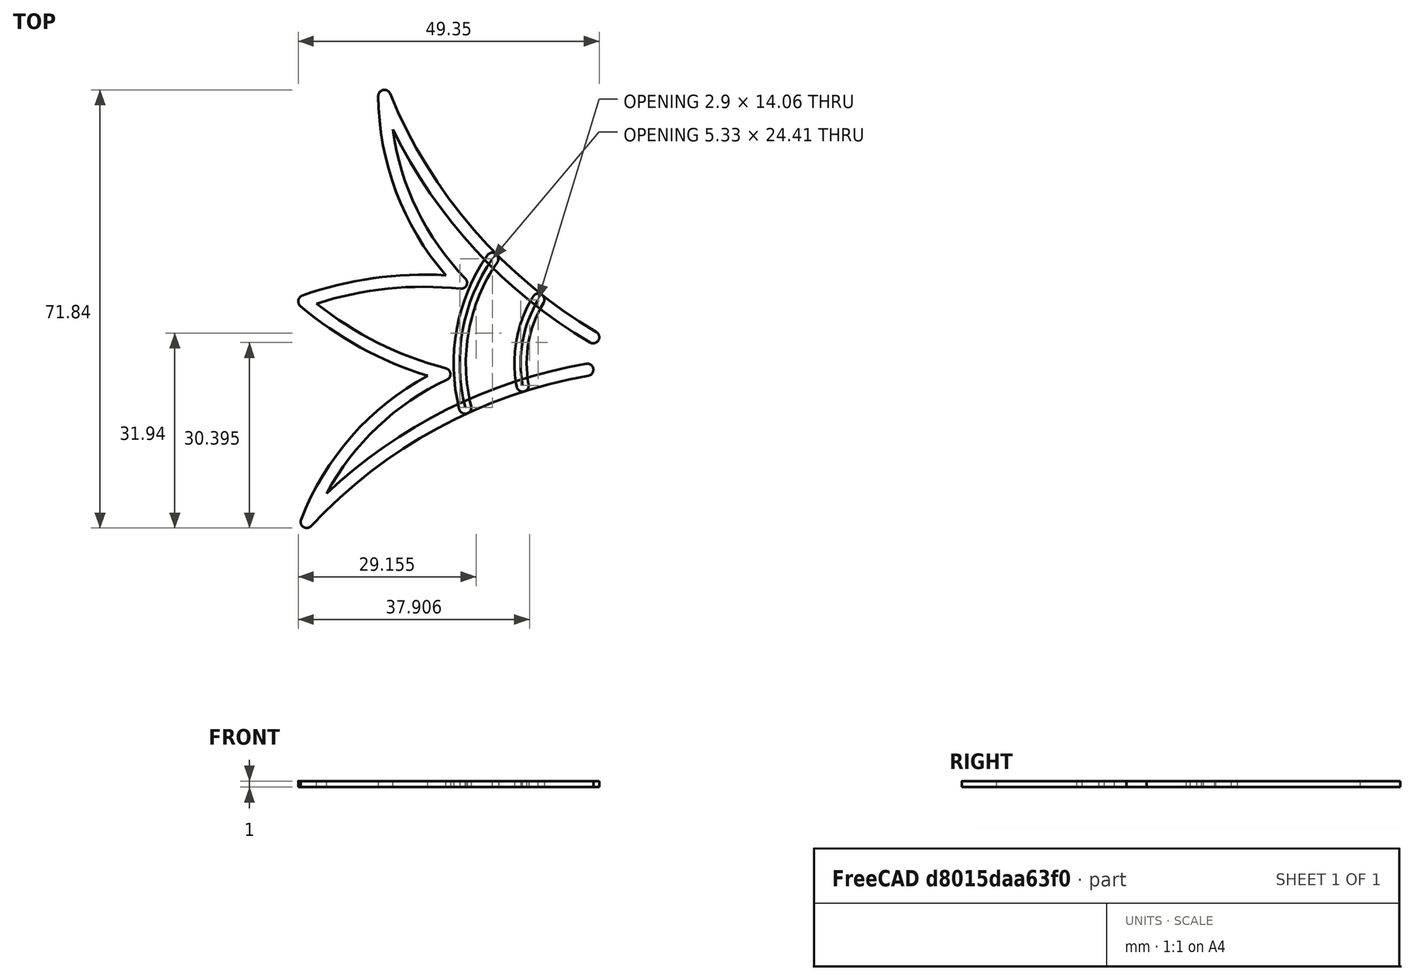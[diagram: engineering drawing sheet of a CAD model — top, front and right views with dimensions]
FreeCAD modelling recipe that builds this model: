
FCSTD DOCUMENT  (FreeCAD 0.20R27319 (Git))
Label: Bookend_1
License: All rights reserved
LicenseURL: http://en.wikipedia.org/wiki/All_rights_reserved
objects: Sketcher::SketchObject×2, TechDraw::DrawViewDimension×2, PartDesign::Body×1, PartDesign::Pad×1, Part::Offset2D×1, Part::Extrusion×1, PartDesign::Plane×1, Part::Mirroring×1, TechDraw::DrawSVGTemplate×1, TechDraw::DrawViewPart×1, TechDraw::DrawPage×1
note: 9 computed .brp shape members not serialized (recipe doc carries the construction recipe); baked Part::Feature solids carry a one-line shape summary decoded from their .brp

FEATURE [PartDesign::Body] Body001  label="Body"
  Origin = -> Origin001
FEATURE [Sketcher::SketchObject] Sketch001
  FullyConstrained = true
  MapMode = 5
  Support = -> [XY_Plane001]
  sketch-geometry (13):
    g0: LineSegment StartX=0 StartY=0 StartZ=0 EndX=150 EndY=-9e-16 EndZ=0
    g1: LineSegment StartX=0 StartY=0 StartZ=0 EndX=0 EndY=150 EndZ=0
    g2: LineSegment StartX=0 StartY=150 StartZ=0 EndX=150 EndY=0 EndZ=0
    g3: LineSegment StartX=0 StartY=0 StartZ=0 EndX=79.9497 EndY=79.9497 EndZ=0
    g4: GeomPoint X=29.9813 Y=120.019 Z=0
    g5: GeomPoint X=90.0373 Y=59.9627 Z=0
    g6: GeomPoint X=120.019 Y=29.9813 Z=0
    g7: ArcOfCircle CenterX=54.6331 CenterY=54.6331 CenterZ=0 NormalX=0 NormalY=0 NormalZ=1 AngleXU=0 Radius=35.8031 StartAngle=0.149412 EndAngle=1.42138
    g8: ArcOfCircle CenterX=125.429 CenterY=65.3732 CenterZ=0 NormalX=0 NormalY=0 NormalZ=1 AngleXU=0 Radius=35.8031 StartAngle=3.29329 EndAngle=4.56069
    g9: ArcOfCircle CenterX=114.608 CenterY=-5.41059 CenterZ=0 NormalX=0 NormalY=0 NormalZ=1 AngleXU=0 Radius=35.8031 StartAngle=0.151702 EndAngle=1.41909
    g10: ArcOfCircle CenterX=65.3732 CenterY=125.429 CenterZ=0 NormalX=0 NormalY=0 NormalZ=1 AngleXU=0 Radius=35.8031 StartAngle=3.29329 EndAngle=4.56069
    g11: ArcOfCircle CenterX=-5.41059 CenterY=114.608 CenterZ=0 NormalX=0 NormalY=0 NormalZ=1 AngleXU=0 Radius=35.8031 StartAngle=0.151702 EndAngle=1.41909
    g12: LineSegment StartX=75 StartY=75 StartZ=0 EndX=79.9497 EndY=79.9497 EndZ=0
  constraints (35):
    c: Coincident(g0,g-1)
    c: PointOnObject(g0,g-1)
    c: Distance(g0) = 150
    c: Coincident(g1,g0)
    c: PointOnObject(g1,g-2)
    c: Distance(g1) = 150
    c: Coincident(g2,g1)
    c: Coincident(g2,g0)
    c: Coincident(g3,g0)
    c: Angle(g0,g3) = 0.785398
    c: PointOnObject(g4,g2)
    c: Distance(g4,g1) = 42.4
    c: PointOnObject(g5,g2)
    c: PointOnObject(g6,g2)
    c: Distance(g5,g6) = 42.4
    c: Coincident(g7,g5)
    c: Coincident(g9,g0)
    c: Coincident(g11,g1)
    c: Coincident(g11,g4)
    c: Coincident(g5,g8)
    c: Coincident(g9,g8)
    c: Coincident(g8,g6)
    c: Coincident(g4,g10)
    c: Coincident(g10,g7)
    c: PointOnObject(g7,g2)
    c: Equal(g11,g10)
    c: Equal(g10,g7)
    c: Equal(g7,g8)
    c: Equal(g8,g9)
    c: Symmetric(g10,g8,g3)
    c: PointOnObject(g12,g3)
    c: PointOnObject(g12,g7)
    c: PointOnObject(g12,g2)
    c: Distance(g12,g12) = 7
    c: Coincident(g3,g12)
FEATURE [PartDesign::Pad] Pad
  Direction = (0,0,1)
  Length = 10
  Length2 = 10
  Profile = -> Sketch001
  ReferenceAxis = -> Sketch001 [N_Axis]
  Type = 0
FEATURE [Sketcher::SketchObject] Sketch
  ExternalGeometry = -> [Sketch001]
  FullyConstrained = false
  MapMode = 5
  Placement = pos=(0,0,10) rot=(0,0,1;0rad)
  Support = -> [Pad]
  sketch-geometry (13):
    g0: LineSegment StartX=0 StartY=150 StartZ=0 EndX=150 EndY=0 EndZ=0
    g1: LineSegment StartX=0 StartY=0 StartZ=0 EndX=75 EndY=75 EndZ=0
    g2: LineSegment StartX=77 StartY=0 StartZ=0 EndX=65.7983 EndY=59.5038 EndZ=0
    g3: ArcOfCircle CenterX=21.5521 CenterY=23.2682 CenterZ=0 NormalX=0 NormalY=0 NormalZ=1 AngleXU=0 Radius=57.9689 StartAngle=5.94509 EndAngle=6.39511
    g4: ArcOfCircle CenterX=109.889 CenterY=61.6651 CenterZ=0 NormalX=0 NormalY=0 NormalZ=1 AngleXU=0 Radius=44.31 StartAngle=3.94601 EndAngle=4.71162
    g5: ArcOfCircle CenterX=140.644 CenterY=93.6374 CenterZ=0 NormalX=0 NormalY=0 NormalZ=1 AngleXU=0 Radius=82.2616 StartAngle=3.6814 EndAngle=4.32876
    g6: ArcOfCircle CenterX=120.192 CenterY=41.8372 CenterZ=0 NormalX=0 NormalY=0 NormalZ=1 AngleXU=0 Radius=57.9689 StartAngle=3.40181 EndAngle=3.85183
    g7: ArcOfCircle CenterX=23.9401 CenterY=45.4852 CenterZ=0 NormalX=0 NormalY=0 NormalZ=1 AngleXU=0 Radius=44.31 StartAngle=5.08531 EndAngle=5.85092
    g8: ArcOfCircle CenterX=-16.3356 CenterY=64.0858 CenterZ=0 NormalX=0 NormalY=0 NormalZ=1 AngleXU=0 Radius=82.2616 StartAngle=5.46816 EndAngle=6.11552
    g9: ArcOfCircle CenterX=65.7983 CenterY=59.5038 CenterZ=0 NormalX=0 NormalY=0 NormalZ=1 AngleXU=0 Radius=20.0707 StartAngle=4.53436 EndAngle=5.26256
    g10: ArcOfCircle CenterX=65.7983 CenterY=59.5038 CenterZ=0 NormalX=0 NormalY=0 NormalZ=1 AngleXU=0 Radius=20.0707 StartAngle=4.53436 EndAngle=5.26256
    g11: ArcOfCircle CenterX=65.7983 CenterY=59.5038 CenterZ=0 NormalX=0 NormalY=0 NormalZ=1 AngleXU=0 Radius=30.0524 StartAngle=4.47297 EndAngle=5.32396
    g12: ArcOfCircle CenterX=65.7983 CenterY=59.5038 CenterZ=0 NormalX=0 NormalY=0 NormalZ=1 AngleXU=0 Radius=30.0524 StartAngle=4.47297 EndAngle=5.32396
  constraints (30):
    c: Coincident(g0,g-3)
    c: Coincident(g0,g-4)
    c: Coincident(g1,g-1)
    c: PointOnObject(g1,g0)
    c: Perpendicular(g0,g1)
    c: PointOnObject(g2,g-1)
    c: DistanceX(g1,g2) = 77
    c: Coincident(g4,g3)
    c: Coincident(g5,g4)
    c: Coincident(g6,g3)
    c: Coincident(g7,g6)
    c: Symmetric(g6,g3,g2)
    c: Coincident(g8,g7)
    c: Symmetric(g8,g5,g2)
    c: Symmetric(g6,g3,g2)
    c: Symmetric(g4,g7,g2)
    c: Symmetric(g8,g5,g2)
    c: PointOnObject(g2,g8)
    c: Coincident(g9,g2)
    c: PointOnObject(g9,g8)
    c: PointOnObject(g9,g5)
    c: Coincident(g10,g9)
    c: Coincident(g10,g9)
    c: Coincident(g10,g9)
    c: Coincident(g11,g9)
    c: PointOnObject(g11,g8)
    c: PointOnObject(g11,g5)
    c: Coincident(g12,g9)
    c: Coincident(g12,g11)
    c: Coincident(g12,g11)
FEATURE [Part::Offset2D] Offset2D
  Fill = true
  Intersection = false
  Join = 0
  Mode = 1
  SelfIntersection = false
  Source = -> Sketch
  Value = 1
FEATURE [Part::Extrusion] Extrude
  Base = -> Offset2D
  Dir = (0,0,1)
  DirMode = 2
  FaceMakerClass = Part::FaceMakerBullseye
  LengthFwd = 1
  LengthRev = 0
  Solid = false
  Symmetric = false
FEATURE [PartDesign::Plane] DatumPlane
  AttachmentOffset = pos=(0,0,0) rot=(0,1,0;0.785398rad)
  Length = 283.998
  MapMode = 5
  Placement = pos=(0,0,0) rot=(0.862856,0.357407,0.357407;1.71777rad)
  ResizeMode = 0
  Support = -> [Pad]
  Width = 90.9045
FEATURE [Part::Mirroring] mirror  label="Extrude (mirrored) "
  Base = (97.6957,97.3989,0)
  Normal = (-0.709153,0.705054,0)
  Source = -> Extrude
FEATURE [TechDraw::DrawSVGTemplate] Template
  EditableTexts = Designed_by_Name=Designed by Name; Drawing_number=Drawing number; FC-Date=Date; FC-SC=Scale; FC-SH=Sheet; FC-Title=Title; Subtitle=Subtitle; Weight=Weight
  Height = 210
  Orientation = 1
  Width = 297
FEATURE [TechDraw::DrawViewPart] View
  CoarseView = false
  Direction = (0,0,1)
  Focus = 100
  HardHidden = false
  IsoCount = 0
  IsoHidden = false
  IsoVisible = false
  LockPosition = false
  Perspective = false
  Rotation = 0
  ScaleType = 0
  SeamHidden = false
  SeamVisible = true
  SmoothHidden = false
  SmoothVisible = true
  Source = -> [mirror,Pad,Extrude]
  X = 103.649
  XDirection = (1,0,0)
  Y = 114.208
FEATURE [TechDraw::DrawViewDimension] Dimension
  AngleOverride = false
  Arbitrary = false
  ArbitraryTolerances = false
  EqualTolerance = true
  ExtensionAngle = 0
  FormatSpec = %.2f
  FormatSpecOverTolerance = %+.2f
  FormatSpecUnderTolerance = %+.2f
  Inverted = false
  LineAngle = 0
  LockPosition = false
  MeasureType = 1
  OverTolerance = 0
  References2D = -> [View]
  Rotation = 0
  ScaleType = 0
  TheoreticalExact = false
  Type = 2
  UnderTolerance = 0
  X = -84.4902
  Y = 0.059652
FEATURE [TechDraw::DrawViewDimension] Dimension001
  AngleOverride = false
  Arbitrary = false
  ArbitraryTolerances = false
  EqualTolerance = true
  ExtensionAngle = 0
  FormatSpec = %.2f
  FormatSpecOverTolerance = %+.2f
  FormatSpecUnderTolerance = %+.2f
  Inverted = false
  LineAngle = 0
  LockPosition = false
  MeasureType = 1
  OverTolerance = 0
  References2D = -> [View]
  Rotation = 0
  ScaleType = 0
  TheoreticalExact = false
  Type = 1
  UnderTolerance = 0
  X = 0
  Y = -89.3113
FEATURE [TechDraw::DrawPage] Page
  KeepUpdated = true
  NextBalloonIndex = 1
  ProjectionType = 0
  Template = -> Template
  Views = -> [View,Dimension,Dimension001]
